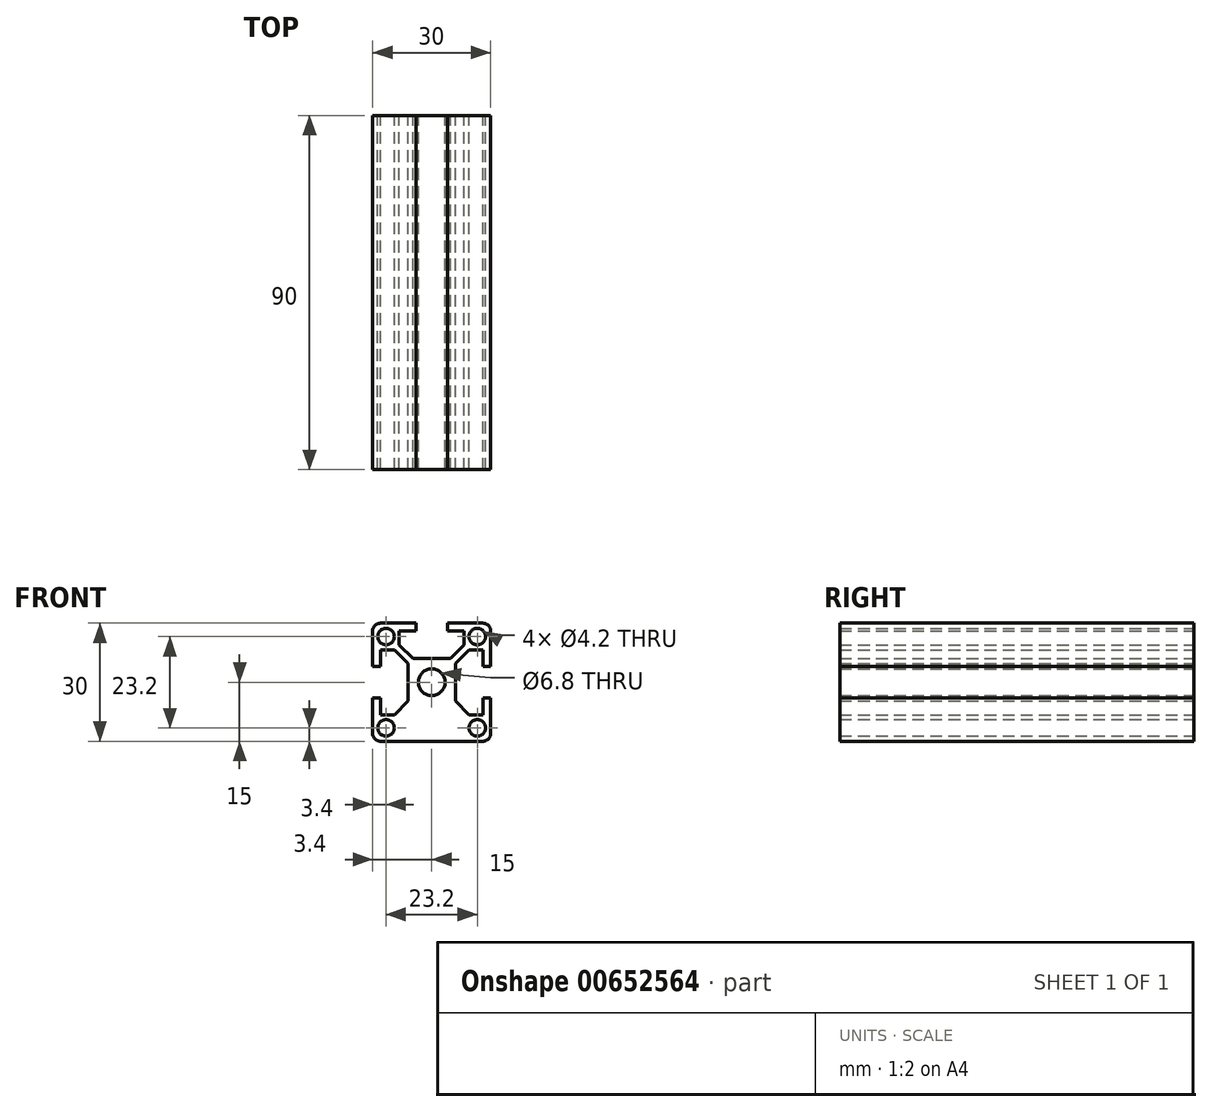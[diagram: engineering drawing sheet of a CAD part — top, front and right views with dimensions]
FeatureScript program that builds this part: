
annotation { "Feature Type Name" : "Feature", "Feature Type Description" : "" }
export const myFeature = defineFeature(function(context is Context, id is Id, definition is map)
    precondition{}
    {
        {
            var Q0;
            Q0=qCreatedBy(makeId("Front.planeOp"),FACE);
            var sketch = newSketch(context, id + "F0", { "sketchPlane" : qUnion([Q0])});
            skLineSegment(sketch, "E0.bottom", {"start": v(15, 15) * mm, "end": v(-15, 15) * mm});
            skLineSegment(sketch, "E0.top", {"start": v(15, -15) * mm, "end": v(-15, -15) * mm});
            skLineSegment(sketch, "E0.left", {"start": v(15, 15) * mm, "end": v(15, -15) * mm});
            skLineSegment(sketch, "E0.right", {"start": v(-15, 15) * mm, "end": v(-15, -15) * mm});
            skPoint(sketch, "E0.middle", {"position": v(0, 0) * mm});
            skLineSegment(sketch, "E1", {"start": v(-4, 15) * mm, "end": v(-4, 13) * mm});
            skLineSegment(sketch, "E2", {"start": v(-4, 13) * mm, "end": v(-8.25, 13) * mm});
            skLineSegment(sketch, "E3", {"start": v(-8.25, 13) * mm, "end": v(-8.25, 9.5) * mm});
            skLineSegment(sketch, "E4", {"start": v(-8.25, 9.5) * mm, "end": v(-4.75, 6) * mm});
            skLineSegment(sketch, "E5", {"start": v(-4.75, 6) * mm, "end": v(4.75, 6) * mm});
            skLineSegment(sketch, "E6", {"start": v(4.75, 6) * mm, "end": v(8.25, 9.5) * mm});
            skLineSegment(sketch, "E7", {"start": v(8.25, 9.5) * mm, "end": v(8.25, 13) * mm});
            skLineSegment(sketch, "E8", {"start": v(8.25, 13) * mm, "end": v(4, 13) * mm});
            skLineSegment(sketch, "E9", {"start": v(4, 13) * mm, "end": v(4, 15) * mm});
            skSolve(sketch);
        }
        {
            var Q0;
            Q0=makeQuery(id+"F0.imprint","IMPRINT",FACE,{"disambiguationData":[TD([[makeQuery(id+"F0.imprint","IMPRINT",EDGE,{"derivedFrom":sQuery(id+"F0.wireOp",EDGE,"E0.top")}),-1.0]])]});
            var Q1;
            {var subQ0=sQuery(id+"F0.wireOp",EDGE,"E1");Q1=makeQuery(id+"F0.imprint","IMPRINT",FACE,{"disambiguationData":[TD([[makeQuery(id+"F0.imprint","IMPRINT",EDGE,{"derivedFrom":subQ0}),1.0]])]});}
            extrude(context, id + "F1", {"entities" : qUnion([Q0, Q1]), "depth" : 90 * mm, "offsetDistance" : 25 * mm});
        }
        {
            var Q0;
            {var subQ0=sQuery(id+"F0.wireOp",EDGE,"E1");Q0=makeQuery(id+"F0.imprint","IMPRINT",FACE,{"disambiguationData":[TD([[makeQuery(id+"F0.imprint","IMPRINT",EDGE,{"derivedFrom":subQ0}),1.0]])]});}
            extrude(context, id + "F2", {"entities" : qUnion([Q0]), "operationType" : NewBodyOperationType.REMOVE, "depth" : 400 * mm, "offsetDistance" : 25 * mm});
        }
        {
            var Q0;
            Q0=makeQuery(id+"F1.opExtrude","CAP_FACE",FACE,{"disambiguationData":[OSD([sQuery(id+"F0.wireOp",EDGE,"E0.bottom"),sQuery(id+"F0.wireOp",EDGE,"E0.top"),sQuery(id+"F0.wireOp",EDGE,"E0.left"),sQuery(id+"F0.wireOp",EDGE,"E0.right")])],"isStart":true});
            var sketch = newSketch(context, id + "F3", { "sketchPlane" : qUnion([Q0])});
            skLineSegment(sketch, "E10.bottom", {"start": v(-9.5, 8.25) * mm, "end": v(-13, 8.25) * mm});
            skLineSegment(sketch, "E10.top", {"start": v(-9.5, -8.25) * mm, "end": v(-13, -8.25) * mm});
            skLineSegment(sketch, "E10.left", {"start": v(-6, 4.75) * mm, "end": v(-6, -4.75) * mm});
            skLineSegment(sketch, "E10.right", {"start": v(-13, 8.25) * mm, "end": v(-13, -8.25) * mm});
            skLineSegment(sketch, "E11.bottom", {"start": v(-13, 4) * mm, "end": v(-31.65, 4) * mm});
            skLineSegment(sketch, "E11.top", {"start": v(-13, -4) * mm, "end": v(-31.65, -4) * mm});
            skLineSegment(sketch, "E11.left", {"start": v(-13, 4) * mm, "end": v(-13, -4) * mm});
            skLineSegment(sketch, "E11.right", {"start": v(-31.65, 4) * mm, "end": v(-31.65, -4) * mm});
            skLineSegment(sketch, "E12.bottom", {"start": v(9.5, 8.25) * mm, "end": v(13, 8.25) * mm});
            skLineSegment(sketch, "E12.top", {"start": v(9.5, -8.25) * mm, "end": v(13, -8.25) * mm});
            skLineSegment(sketch, "E12.left", {"start": v(6, 4.75) * mm, "end": v(6, -4.75) * mm});
            skLineSegment(sketch, "E12.right", {"start": v(13, 8.25) * mm, "end": v(13, -8.25) * mm});
            skLineSegment(sketch, "E13.bottom", {"start": v(13, 4) * mm, "end": v(32.96, 4) * mm});
            skLineSegment(sketch, "E13.top", {"start": v(13, -4) * mm, "end": v(32.96, -4) * mm});
            skLineSegment(sketch, "E13.left", {"start": v(13, 4) * mm, "end": v(13, -4) * mm});
            skLineSegment(sketch, "E13.right", {"start": v(32.96, 4) * mm, "end": v(32.96, -4) * mm});
            skCircle(sketch, "E14", {"center": v(0, 0) * mm, "radius": 3.4 * mm});
            skCircle(sketch, "E15", {"center": v(-11.6, 11.6) * mm, "radius": 2.1 * mm});
            skCircle(sketch, "E16", {"center": v(-11.6, -11.6) * mm, "radius": 2.1 * mm});
            skCircle(sketch, "E17", {"center": v(11.6, -11.6) * mm, "radius": 2.1 * mm});
            skCircle(sketch, "E18", {"center": v(11.6, 11.6) * mm, "radius": 2.1 * mm});
            skLineSegment(sketch, "E19", {"start": v(-9.5, 8.25) * mm, "end": v(-6, 4.75) * mm});
            skLineSegment(sketch, "E20", {"start": v(-9.5, -8.25) * mm, "end": v(-6, -4.75) * mm});
            skPoint(sketch, "E21.orphan", {"position": v(-6, 8.25) * mm});
            skPoint(sketch, "E22.orphan", {"position": v(-6, -8.25) * mm});
            skLineSegment(sketch, "E23", {"start": v(9.5, 8.25) * mm, "end": v(6, 4.75) * mm});
            skLineSegment(sketch, "E24", {"start": v(9.5, -8.25) * mm, "end": v(6, -4.75) * mm});
            skPoint(sketch, "E25.orphan", {"position": v(6, 8.25) * mm});
            skPoint(sketch, "E26.orphan", {"position": v(6, -8.25) * mm});
            skSolve(sketch);
        }
        {
            var Q0;
            Q0 = qSketchRegion(id + "F3", true);
            extrude(context, id + "F4", {"entities" : qUnion([Q0]), "operationType" : NewBodyOperationType.REMOVE, "oppositeDirection" : true, "depth" : 90 * mm, "offsetDistance" : 25 * mm});
        }
        {
            var Q0;
            Q0=makeQuery(id+"F1.opExtrude","SWEPT_EDGE",EDGE,{"disambiguationData":[OSD([sQuery(id+"F0.wireOp",EDGE,"E0.bottom"),sQuery(id+"F0.wireOp",EDGE,"E0.right")])]});
            var Q1;
            Q1=makeQuery(id+"F1.opExtrude","SWEPT_EDGE",EDGE,{"disambiguationData":[OSD([sQuery(id+"F0.wireOp",EDGE,"E0.top"),sQuery(id+"F0.wireOp",EDGE,"E0.right")])]});
            var Q2;
            Q2=makeQuery(id+"F1.opExtrude","SWEPT_EDGE",EDGE,{"disambiguationData":[OSD([sQuery(id+"F0.wireOp",EDGE,"E0.top"),sQuery(id+"F0.wireOp",EDGE,"E0.left")])]});
            var Q3;
            Q3=makeQuery(id+"F1.opExtrude","SWEPT_EDGE",EDGE,{"disambiguationData":[OSD([sQuery(id+"F0.wireOp",EDGE,"E0.bottom"),sQuery(id+"F0.wireOp",EDGE,"E0.left")])]});
            fillet(context, id + "F5", {"entities" : qUnion([Q0, Q1, Q2, Q3]), "radius" : 2 * mm, "tangentPropagation" : true, "allowEdgeOverflow" : false});
        }
    });
